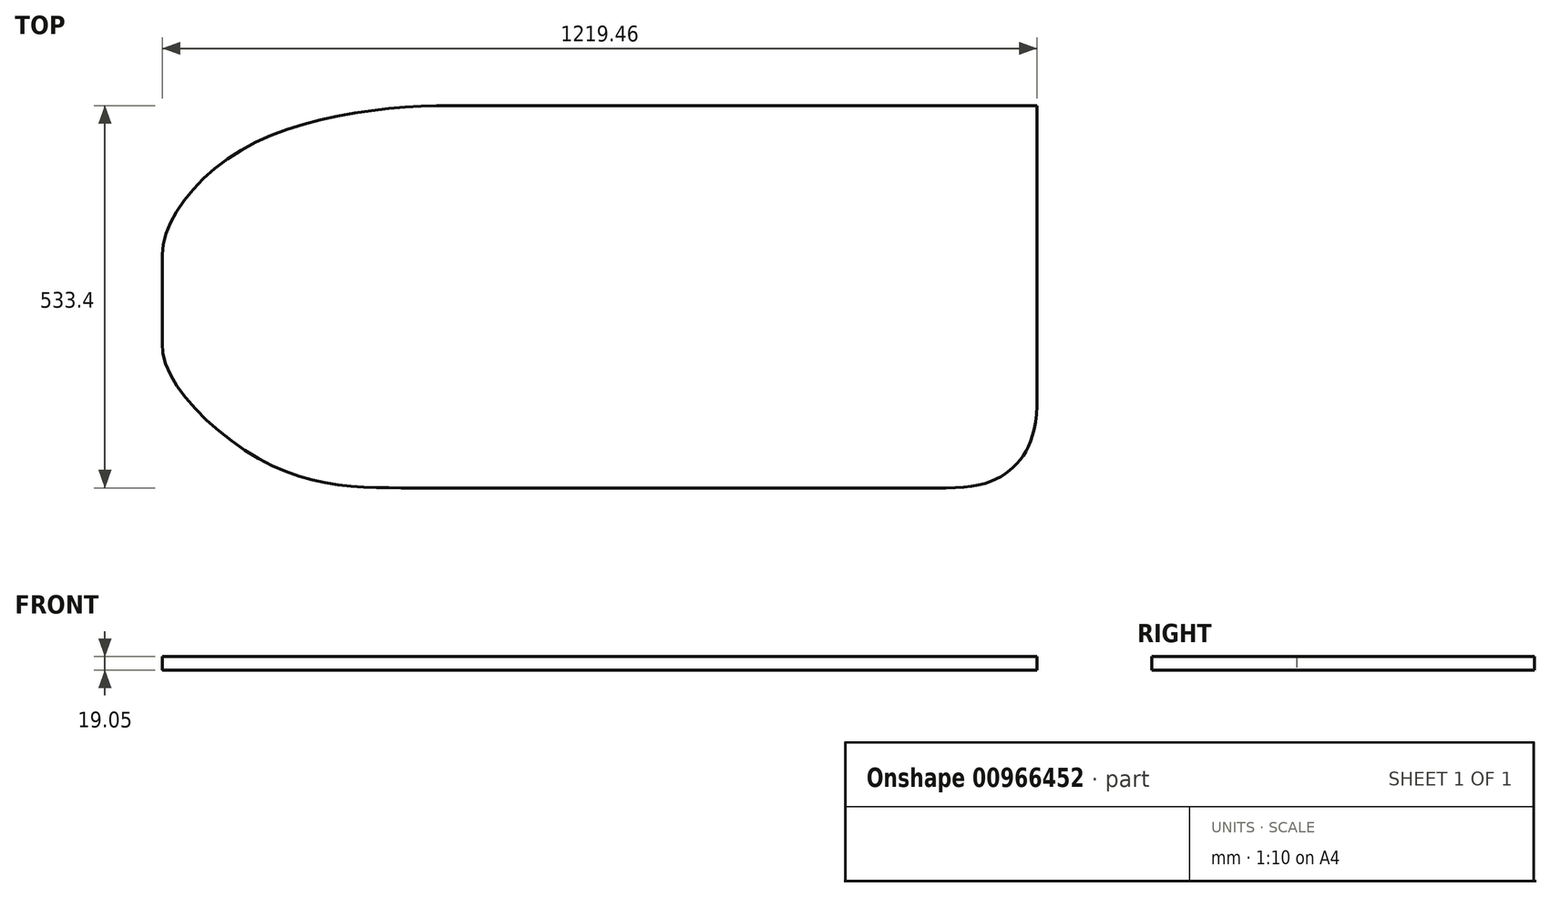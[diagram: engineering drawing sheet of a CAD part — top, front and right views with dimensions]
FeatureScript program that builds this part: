
annotation { "Feature Type Name" : "Feature", "Feature Type Description" : "" }
export const myFeature = defineFeature(function(context is Context, id is Id, definition is map)
    precondition{}
    {
        {
            var Q0;
            Q0=qCreatedBy(makeId("Top.planeOp"),FACE);
            var sketch = newSketch(context, id + "F0", { "sketchPlane" : qUnion([Q0])});
            skLineSegment(sketch, "E0.bottom", {"start": v(254.35, -8.3) * mm, "end": v(1071.02, -8.3) * mm});
            skLineSegment(sketch, "E0.top", {"start": v(201.34, -541.7) * mm, "end": v(944.02, -541.7) * mm});
            skLineSegment(sketch, "E0.left", {"start": v(-148.18, -216.27) * mm, "end": v(-148.18, -339.82) * mm});
            skLineSegment(sketch, "E0.right", {"start": v(1071.02, -8.3) * mm, "end": v(1071.02, -414.7) * mm});
            skFitSpline(sketch, "E1", {"points": [v(-148.18, -216.27) * mm, v(-34.99, -68.39) * mm, v(254.35, -8.3) * mm], "startDerivative": vector(-3.11, 319.2) * mm, "endDerivative": vector(458.27, 0.88) * mm});
            skFitSpline(sketch, "E2", {"points": [v(-148.18, -339.82) * mm, v(0, -508.29) * mm, v(201.34, -541.7) * mm], "startDerivative": vector(-31.13, -306.9) * mm, "endDerivative": vector(390.37, -3.46) * mm});
            skFitSpline(sketch, "E3", {"points": [v(944.02, -541.7) * mm, v(1040.5, -510) * mm, v(1071.02, -414.7) * mm], "startDerivative": vector(309.6, 0) * mm, "endDerivative": vector(0, 304.76) * mm});
            skPoint(sketch, "E4.orphan", {"position": v(1071.02, -541.7) * mm});
            skSolve(sketch);
        }
        {
            var Q0;
            Q0 = qSketchRegion(id + "F0", true);
            extrude(context, id + "F1", {"entities" : qUnion([Q0]), "depth" : 19.05 * mm, "offsetDistance" : 25.4 * mm});
        }
    });
